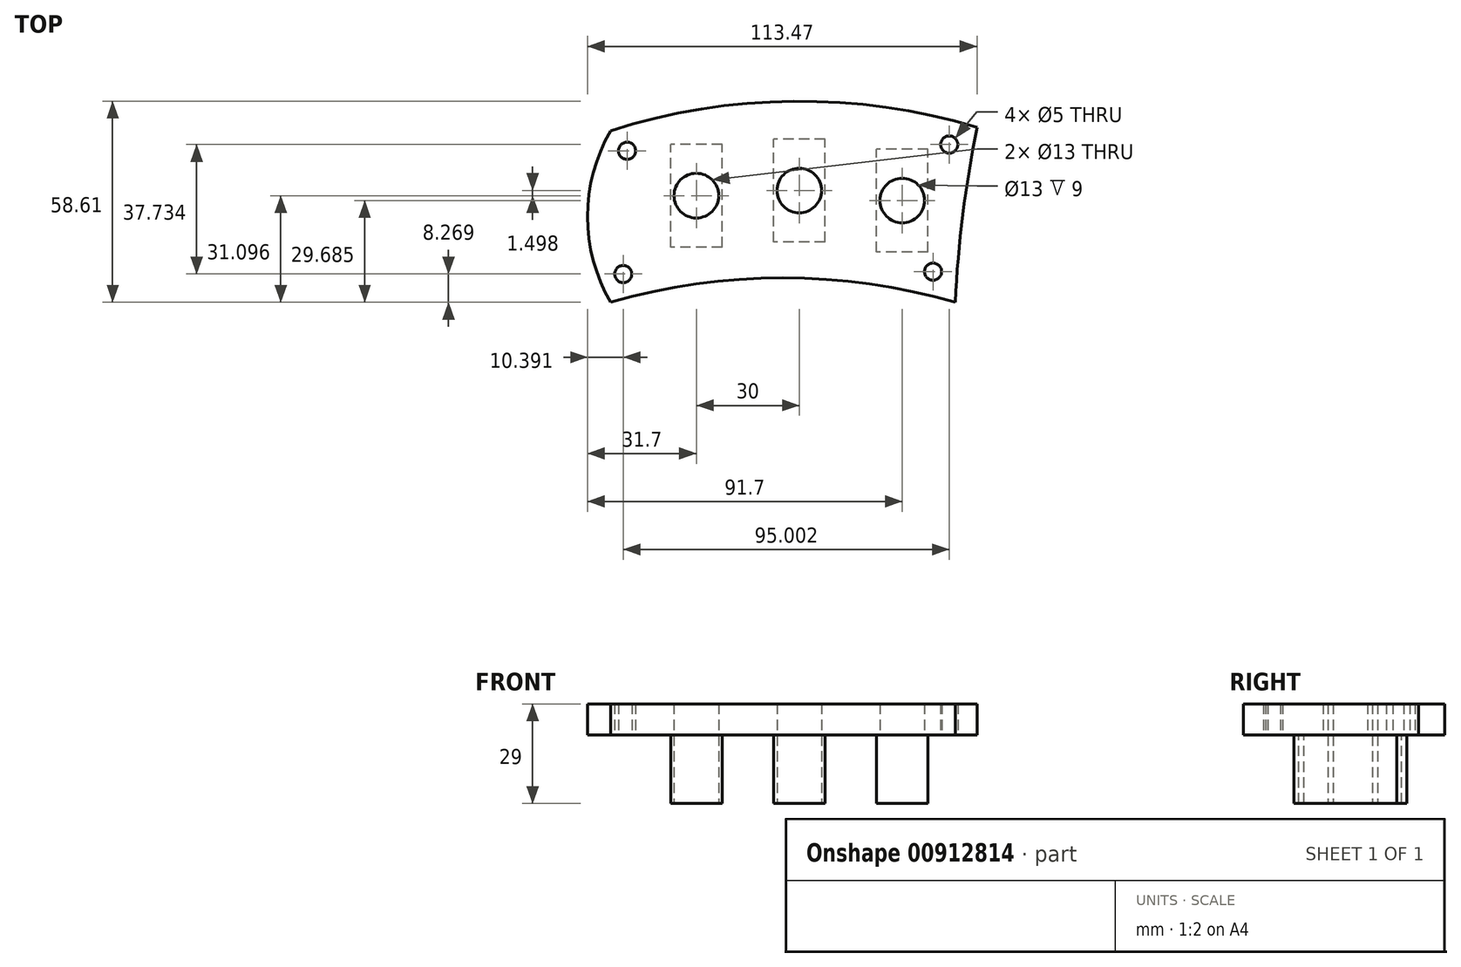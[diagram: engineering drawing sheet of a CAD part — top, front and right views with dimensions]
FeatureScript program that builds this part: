
annotation { "Feature Type Name" : "Feature", "Feature Type Description" : "" }
export const myFeature = defineFeature(function(context is Context, id is Id, definition is map)
    precondition{}
    {
        {
            var Q0;
            Q0=qCreatedBy(makeId("Top.planeOp"),FACE);
            var sketch = newSketch(context, id + "F0", { "sketchPlane" : qUnion([Q0])});
            skCircle(sketch, "E0", {"center": v(0, 0) * mm, "radius": 42.86 * mm, "construction": true});
            skLineSegment(sketch, "E1.bottom", {"start": v(70, 70) * mm, "end": v(-70, 70) * mm, "construction": true});
            skLineSegment(sketch, "E1.top", {"start": v(70, -70) * mm, "end": v(-70, -70) * mm, "construction": true});
            skLineSegment(sketch, "E1.left", {"start": v(70, 70) * mm, "end": v(70, -70) * mm, "construction": true});
            skLineSegment(sketch, "E1.right", {"start": v(-70, 70) * mm, "end": v(-70, -70) * mm, "construction": true});
            skArc(sketch, "E2", {"start": v(70, 70) * mm, "mid": v(0, 88.76) * mm, "end": v(-70, 70) * mm});
            skArc(sketch, "E3", {"start": v(-88.29, 11.48) * mm, "mid": v(-85.36, -30.66) * mm, "end": v(-70, -70) * mm});
            skArc(sketch, "E4", {"start": v(-70, -70) * mm, "mid": v(0, -88.76) * mm, "end": v(70, -70) * mm});
            skArc(sketch, "E5", {"start": v(70, -70) * mm, "mid": v(85.36, -30.66) * mm, "end": v(88.29, 11.48) * mm});
            skLineSegment(sketch, "E6.bottom", {"start": v(55, 55) * mm, "end": v(-55, 55) * mm, "construction": true});
            skLineSegment(sketch, "E6.top", {"start": v(55, -55) * mm, "end": v(-55, -55) * mm, "construction": true});
            skLineSegment(sketch, "E6.left", {"start": v(55, 55) * mm, "end": v(55, -55) * mm, "construction": true});
            skLineSegment(sketch, "E6.right", {"start": v(-55, 55) * mm, "end": v(-55, -55) * mm, "construction": true});
            skCircle(sketch, "E7", {"center": v(-55, 55) * mm, "radius": 2.5 * mm});
            skArc(sketch, "E8", {"start": v(-59.61, 49.09) * mm, "mid": v(-49.7, 49.7) * mm, "end": v(-49.09, 59.61) * mm});
            skCircle(sketch, "E9", {"center": v(55, 55) * mm, "radius": 2.5 * mm});
            skArc(sketch, "E10", {"start": v(49.09, 59.61) * mm, "mid": v(49.7, 49.7) * mm, "end": v(59.61, 49.09) * mm});
            skArc(sketch, "E11", {"start": v(-49.09, -59.61) * mm, "mid": v(-49.7, -49.7) * mm, "end": v(-59.61, -49.09) * mm});
            skCircle(sketch, "E12", {"center": v(-55, -55) * mm, "radius": 2.5 * mm});
            skArc(sketch, "E13", {"start": v(59.61, -49.09) * mm, "mid": v(49.7, -49.7) * mm, "end": v(49.09, -59.61) * mm});
            skCircle(sketch, "E14", {"center": v(55, -55) * mm, "radius": 2.5 * mm});
            skArc(sketch, "E15.0", {"start": v(47.87, 64.23) * mm, "mid": v(0, 73.76) * mm, "end": v(-47.87, 64.23) * mm});
            skArc(sketch, "E15.1", {"start": v(64.23, -47.87) * mm, "mid": v(73.76, 0) * mm, "end": v(64.23, 47.87) * mm});
            skArc(sketch, "E15.2", {"start": v(-47.87, -64.23) * mm, "mid": v(0, -73.76) * mm, "end": v(47.87, -64.23) * mm});
            skArc(sketch, "E15.3", {"start": v(-64.23, 47.87) * mm, "mid": v(-73.76, 0) * mm, "end": v(-64.23, -47.87) * mm});
            skArc(sketch, "E16", {"start": v(109.94, -69.44) * mm, "mid": v(105.48, -27.66) * mm, "end": v(94.08, 12.78) * mm});
            skArc(sketch, "E17.0", {"start": v(209.56, -57.5) * mm, "mid": v(193.7, 30.58) * mm, "end": v(156, 111.76) * mm});
            skCircle(sketch, "E18.0", {"center": v(-140, -75) * mm, "radius": 300 * mm, "construction": true});
            skCircle(sketch, "E19", {"center": v(132.72, 50) * mm, "radius": 26.2 * mm, "construction": true});
            skCircle(sketch, "E20", {"center": v(155.8, -25) * mm, "radius": 26.2 * mm, "construction": true});
            skArc(sketch, "E21", {"start": v(156, 111.76) * mm, "mid": v(104.5, 108.03) * mm, "end": v(69.57, 70) * mm});
            skArc(sketch, "E22", {"start": v(109.94, -69.44) * mm, "mid": v(162.27, -84.5) * mm, "end": v(209.56, -57.5) * mm});
            skLineSegment(sketch, "E23", {"start": v(0, 0) * mm, "end": v(0, 164.88) * mm, "construction": true});
            skPoint(sketch, "E23.endSnap0", {"position": v(0, 55) * mm});
            skLineSegment(sketch, "E24", {"start": v(-22.48, 0) * mm, "end": v(0, 0) * mm, "construction": true});
            skArc(sketch, "E25.MirrorC", {"start": v(-109.94, -69.44) * mm, "mid": v(-105.48, -27.66) * mm, "end": v(-94.08, 12.78) * mm});
            skCircle(sketch, "E26.MirrorC", {"center": v(140, -75) * mm, "radius": 300 * mm, "construction": true});
            skArc(sketch, "E27.MirrorC", {"start": v(-209.56, -57.5) * mm, "mid": v(-193.7, 30.58) * mm, "end": v(-156, 111.76) * mm});
            skArc(sketch, "E28.MirrorC", {"start": v(-156, 111.76) * mm, "mid": v(-104.5, 108.03) * mm, "end": v(-69.57, 70) * mm});
            skCircle(sketch, "E29.MirrorC", {"center": v(-132.72, 50) * mm, "radius": 26.2 * mm, "construction": true});
            skArc(sketch, "E30.MirrorC", {"start": v(-109.94, -69.44) * mm, "mid": v(-162.27, -84.5) * mm, "end": v(-209.56, -57.5) * mm});
            skCircle(sketch, "E31.MirrorC", {"center": v(-155.8, -25) * mm, "radius": 26.2 * mm, "construction": true});
            skArc(sketch, "E32.0", {"start": v(-136.64, 99.97) * mm, "mid": v(-109.56, 93.79) * mm, "end": v(-88.95, 75.15) * mm});
            skArc(sketch, "E32.1", {"start": v(-193.47, -43.06) * mm, "mid": v(-179.4, 26.06) * mm, "end": v(-151.15, 90.7) * mm});
            skArc(sketch, "E32.2", {"start": v(-133.65, -66.12) * mm, "mid": v(-161.23, -69.52) * mm, "end": v(-186.94, -59) * mm});
            skArc(sketch, "E32.3", {"start": v(-124, -52.1) * mm, "mid": v(-112.65, 4.94) * mm, "end": v(-89.13, 58.13) * mm});
            skArc(sketch, "E33.0", {"start": v(136.64, 99.97) * mm, "mid": v(109.56, 93.79) * mm, "end": v(88.95, 75.15) * mm});
            skArc(sketch, "E33.1", {"start": v(193.47, -43.06) * mm, "mid": v(179.4, 26.06) * mm, "end": v(151.15, 90.7) * mm});
            skArc(sketch, "E33.2", {"start": v(133.65, -66.12) * mm, "mid": v(161.23, -69.52) * mm, "end": v(186.94, -59) * mm});
            skArc(sketch, "E33.3", {"start": v(124, -52.1) * mm, "mid": v(112.65, 4.94) * mm, "end": v(89.13, 58.13) * mm});
            skArc(sketch, "E34.0", {"start": v(-144.5, 96.12) * mm, "mid": v(-110.94, 91.12) * mm, "end": v(-87.6, 66.5) * mm, "construction": true});
            skArc(sketch, "E34.1", {"start": v(-191.15, -51.32) * mm, "mid": v(-176.53, 25.15) * mm, "end": v(-144.5, 96.12) * mm, "construction": true});
            skArc(sketch, "E34.2", {"start": v(-127.57, -59.82) * mm, "mid": v(-160.83, -66.54) * mm, "end": v(-191.15, -51.32) * mm, "construction": true});
            skArc(sketch, "E34.3", {"start": v(-127.57, -59.82) * mm, "mid": v(-115.52, 5.85) * mm, "end": v(-87.6, 66.5) * mm, "construction": true});
            skArc(sketch, "E35.0", {"start": v(144.5, 96.12) * mm, "mid": v(110.94, 91.12) * mm, "end": v(87.6, 66.5) * mm, "construction": true});
            skArc(sketch, "E35.1", {"start": v(191.15, -51.32) * mm, "mid": v(176.53, 25.15) * mm, "end": v(144.5, 96.12) * mm, "construction": true});
            skArc(sketch, "E35.2", {"start": v(127.57, -59.82) * mm, "mid": v(160.83, -66.54) * mm, "end": v(191.15, -51.32) * mm, "construction": true});
            skArc(sketch, "E35.3", {"start": v(127.57, -59.82) * mm, "mid": v(115.52, 5.85) * mm, "end": v(87.6, 66.5) * mm, "construction": true});
            skCircle(sketch, "E36", {"center": v(-144.5, 96.12) * mm, "radius": 2.5 * mm});
            skArc(sketch, "E37", {"start": v(-147.03, 91.8) * mm, "mid": v(-141.79, 91.92) * mm, "end": v(-139.53, 96.65) * mm});
            skCircle(sketch, "E38", {"center": v(-87.6, 66.5) * mm, "radius": 2.5 * mm});
            skArc(sketch, "E39", {"start": v(-90.02, 70.87) * mm, "mid": v(-92.6, 66.59) * mm, "end": v(-90.18, 62.2) * mm});
            skCircle(sketch, "E40", {"center": v(-191.15, -51.32) * mm, "radius": 2.5 * mm});
            skArc(sketch, "E41", {"start": v(-187.4, -54.62) * mm, "mid": v(-186.52, -49.45) * mm, "end": v(-190.74, -46.34) * mm});
            skCircle(sketch, "E42", {"center": v(-127.57, -59.82) * mm, "radius": 2.5 * mm});
            skArc(sketch, "E43", {"start": v(-127.21, -54.83) * mm, "mid": v(-131.71, -57.02) * mm, "end": v(-132.06, -62.01) * mm});
            skCircle(sketch, "E44", {"center": v(87.6, 66.5) * mm, "radius": 2.5 * mm});
            skArc(sketch, "E45", {"start": v(90.18, 62.2) * mm, "mid": v(92.6, 66.59) * mm, "end": v(90.02, 70.87) * mm});
            skCircle(sketch, "E46", {"center": v(144.5, 96.12) * mm, "radius": 2.5 * mm});
            skArc(sketch, "E47", {"start": v(139.53, 96.65) * mm, "mid": v(141.79, 91.92) * mm, "end": v(147.03, 91.8) * mm});
            skCircle(sketch, "E48", {"center": v(127.57, -59.82) * mm, "radius": 2.5 * mm});
            skArc(sketch, "E49", {"start": v(132.06, -62.01) * mm, "mid": v(131.71, -57.02) * mm, "end": v(127.21, -54.83) * mm});
            skCircle(sketch, "E50", {"center": v(191.15, -51.32) * mm, "radius": 2.5 * mm});
            skArc(sketch, "E51", {"start": v(190.74, -46.34) * mm, "mid": v(186.52, -49.45) * mm, "end": v(187.4, -54.62) * mm});
            skPoint(sketch, "E52.visualSharp", {"position": v(-52.66, 62.12) * mm});
            skArc(sketch, "E52.filletArc", {"start": v(-47.87, 64.23) * mm, "mid": v(-49.62, 62.22) * mm, "end": v(-49.09, 59.61) * mm});
            skPoint(sketch, "E53.visualSharp", {"position": v(-62.12, 52.66) * mm});
            skArc(sketch, "E53.filletArc", {"start": v(-59.61, 49.09) * mm, "mid": v(-62.22, 49.62) * mm, "end": v(-64.23, 47.87) * mm});
            skPoint(sketch, "E54.visualSharp", {"position": v(52.66, 62.12) * mm});
            skArc(sketch, "E54.filletArc", {"start": v(49.09, 59.61) * mm, "mid": v(49.62, 62.22) * mm, "end": v(47.87, 64.23) * mm});
            skPoint(sketch, "E55.visualSharp", {"position": v(62.12, 52.66) * mm});
            skArc(sketch, "E55.filletArc", {"start": v(64.23, 47.87) * mm, "mid": v(62.22, 49.62) * mm, "end": v(59.61, 49.09) * mm});
            skPoint(sketch, "E56.visualSharp", {"position": v(-62.12, -52.66) * mm});
            skArc(sketch, "E56.filletArc", {"start": v(-64.23, -47.87) * mm, "mid": v(-62.22, -49.62) * mm, "end": v(-59.61, -49.09) * mm});
            skPoint(sketch, "E57.visualSharp", {"position": v(-52.66, -62.12) * mm});
            skArc(sketch, "E57.filletArc", {"start": v(-49.09, -59.61) * mm, "mid": v(-49.62, -62.22) * mm, "end": v(-47.87, -64.23) * mm});
            skPoint(sketch, "E58.visualSharp", {"position": v(52.66, -62.12) * mm});
            skArc(sketch, "E58.filletArc", {"start": v(47.87, -64.23) * mm, "mid": v(49.62, -62.22) * mm, "end": v(49.09, -59.61) * mm});
            skPoint(sketch, "E59.visualSharp", {"position": v(62.12, -52.66) * mm});
            skArc(sketch, "E59.filletArc", {"start": v(59.61, -49.09) * mm, "mid": v(62.22, -49.62) * mm, "end": v(64.23, -47.87) * mm});
            skPoint(sketch, "E60.visualSharp", {"position": v(-84.1, 35.82) * mm});
            skArc(sketch, "E60.filletArc", {"start": v(-88.29, 11.48) * mm, "mid": v(-90.62, 14.65) * mm, "end": v(-94.08, 12.78) * mm});
            skPoint(sketch, "E61.visualSharp", {"position": v(84.1, 35.82) * mm});
            skArc(sketch, "E61.filletArc", {"start": v(94.08, 12.78) * mm, "mid": v(90.62, 14.65) * mm, "end": v(88.29, 11.48) * mm});
            skPoint(sketch, "E62.visualSharp", {"position": v(86.71, 71.41) * mm});
            skArc(sketch, "E62.filletArc", {"start": v(88.95, 75.15) * mm, "mid": v(88.55, 72.78) * mm, "end": v(90.02, 70.87) * mm});
            skPoint(sketch, "E63.visualSharp", {"position": v(87.13, 61.52) * mm});
            skArc(sketch, "E63.filletArc", {"start": v(90.18, 62.2) * mm, "mid": v(88.82, 60.38) * mm, "end": v(89.13, 58.13) * mm});
            skPoint(sketch, "E64.visualSharp", {"position": v(140.99, 99.67) * mm});
            skArc(sketch, "E64.filletArc", {"start": v(139.53, 96.65) * mm, "mid": v(138.82, 98.94) * mm, "end": v(136.64, 99.97) * mm});
            skPoint(sketch, "E65.visualSharp", {"position": v(149.13, 94.2) * mm});
            skArc(sketch, "E65.filletArc", {"start": v(151.15, 90.7) * mm, "mid": v(149.32, 92.1) * mm, "end": v(147.03, 91.8) * mm});
            skPoint(sketch, "E66.visualSharp", {"position": v(124.32, -56.02) * mm});
            skArc(sketch, "E66.filletArc", {"start": v(124, -52.1) * mm, "mid": v(125.05, -54.12) * mm, "end": v(127.21, -54.83) * mm});
            skPoint(sketch, "E67.visualSharp", {"position": v(129.67, -64.36) * mm});
            skArc(sketch, "E67.filletArc", {"start": v(132.06, -62.01) * mm, "mid": v(131.96, -64.41) * mm, "end": v(133.65, -66.12) * mm});
            skPoint(sketch, "E68.visualSharp", {"position": v(190.32, -56.25) * mm});
            skArc(sketch, "E68.filletArc", {"start": v(186.94, -59) * mm, "mid": v(188.13, -56.9) * mm, "end": v(187.4, -54.62) * mm});
            skPoint(sketch, "E69.visualSharp", {"position": v(193.84, -47.1) * mm});
            skArc(sketch, "E69.filletArc", {"start": v(190.74, -46.34) * mm, "mid": v(192.79, -45.27) * mm, "end": v(193.47, -43.06) * mm});
            skPoint(sketch, "E70.visualSharp", {"position": v(-87.13, 61.52) * mm});
            skArc(sketch, "E70.filletArc", {"start": v(-89.13, 58.13) * mm, "mid": v(-88.82, 60.38) * mm, "end": v(-90.18, 62.2) * mm});
            skPoint(sketch, "E71.visualSharp", {"position": v(-86.71, 71.41) * mm});
            skArc(sketch, "E71.filletArc", {"start": v(-90.02, 70.87) * mm, "mid": v(-88.55, 72.78) * mm, "end": v(-88.95, 75.15) * mm});
            skPoint(sketch, "E72.visualSharp", {"position": v(-140.99, 99.67) * mm});
            skArc(sketch, "E72.filletArc", {"start": v(-136.64, 99.97) * mm, "mid": v(-138.82, 98.94) * mm, "end": v(-139.53, 96.65) * mm});
            skPoint(sketch, "E73.visualSharp", {"position": v(-149.13, 94.2) * mm});
            skArc(sketch, "E73.filletArc", {"start": v(-147.03, 91.8) * mm, "mid": v(-149.32, 92.1) * mm, "end": v(-151.15, 90.7) * mm});
            skPoint(sketch, "E74.visualSharp", {"position": v(-193.84, -47.1) * mm});
            skArc(sketch, "E74.filletArc", {"start": v(-193.47, -43.06) * mm, "mid": v(-192.79, -45.27) * mm, "end": v(-190.74, -46.34) * mm});
            skPoint(sketch, "E75.visualSharp", {"position": v(-190.32, -56.25) * mm});
            skArc(sketch, "E75.filletArc", {"start": v(-187.4, -54.62) * mm, "mid": v(-188.13, -56.9) * mm, "end": v(-186.94, -59) * mm});
            skPoint(sketch, "E76.visualSharp", {"position": v(-129.67, -64.36) * mm});
            skArc(sketch, "E76.filletArc", {"start": v(-133.65, -66.12) * mm, "mid": v(-131.96, -64.41) * mm, "end": v(-132.06, -62.01) * mm});
            skPoint(sketch, "E77.visualSharp", {"position": v(-124.32, -56.02) * mm});
            skArc(sketch, "E77.filletArc", {"start": v(-127.21, -54.83) * mm, "mid": v(-125.05, -54.12) * mm, "end": v(-124, -52.1) * mm});
            skLineSegment(sketch, "E78.bottom", {"start": v(200, -57.5) * mm, "end": v(310, -57.5) * mm, "construction": true});
            skLineSegment(sketch, "E78.top", {"start": v(200, -7.5) * mm, "end": v(310, -7.5) * mm, "construction": true});
            skLineSegment(sketch, "E78.left", {"start": v(200, -57.5) * mm, "end": v(200, -7.5) * mm, "construction": true});
            skLineSegment(sketch, "E78.right", {"start": v(310, -57.5) * mm, "end": v(310, -7.5) * mm, "construction": true});
            skArc(sketch, "E79", {"start": v(310, -7.5) * mm, "mid": v(256.7, 1.1) * mm, "end": v(203.23, -6.5) * mm});
            skArc(sketch, "E80", {"start": v(310, -57.5) * mm, "mid": v(316.7, -32.5) * mm, "end": v(310, -7.5) * mm});
            skPoint(sketch, "E81.centerSnap0", {"position": v(200, -32.5) * mm});
            skPoint(sketch, "E82.centerSnap0", {"position": v(255, -7.5) * mm});
            skArc(sketch, "E83", {"start": v(310, -57.5) * mm, "mid": v(259.78, -50.35) * mm, "end": v(209.56, -57.5) * mm});
            skArc(sketch, "E84.0", {"start": v(317.11, -33.01) * mm, "mid": v(259.78, -24.85) * mm, "end": v(202.45, -33.01) * mm, "construction": true});
            skCircle(sketch, "E85", {"center": v(255, -24.9) * mm, "radius": 6.5 * mm});
            skCircle(sketch, "E86", {"center": v(225, -27.82) * mm, "radius": 6.5 * mm});
            skCircle(sketch, "E87", {"center": v(285, -26.4) * mm, "radius": 6.5 * mm});
            skArc(sketch, "E88.0", {"start": v(216.55, -57.15) * mm, "mid": v(214.25, -30.76) * mm, "end": v(210, -4.6) * mm, "construction": true});
            skArc(sketch, "E89.0", {"start": v(305.2, -13.33) * mm, "mid": v(255.23, -5.89) * mm, "end": v(205.24, -13.2) * mm, "construction": true});
            skArc(sketch, "E89.1", {"start": v(306.3, -49.23) * mm, "mid": v(309.68, -31.16) * mm, "end": v(305.2, -13.33) * mm, "construction": true});
            skArc(sketch, "E89.2", {"start": v(306.3, -49.23) * mm, "mid": v(256.86, -43.37) * mm, "end": v(207.6, -50.78) * mm, "construction": true});
            skCircle(sketch, "E90", {"center": v(211.3, -11.5) * mm, "radius": 2.5 * mm});
            skCircle(sketch, "E91", {"center": v(216.02, -48.54) * mm, "radius": 2.5 * mm});
            skCircle(sketch, "E92", {"center": v(306.3, -49.23) * mm, "radius": 2.5 * mm});
            skCircle(sketch, "E93", {"center": v(305.2, -13.33) * mm, "radius": 2.5 * mm});
            skCircle(sketch, "E94.MirrorC", {"center": v(-225, -27.82) * mm, "radius": 6.5 * mm});
            skCircle(sketch, "E95.MirrorC", {"center": v(-255, -24.9) * mm, "radius": 6.5 * mm});
            skCircle(sketch, "E96.MirrorC", {"center": v(-285, -26.4) * mm, "radius": 6.5 * mm});
            skArc(sketch, "E97.MirrorCS", {"start": v(-306.3, -49.23) * mm, "mid": v(-309.68, -31.16) * mm, "end": v(-305.2, -13.33) * mm, "construction": true});
            skCircle(sketch, "E98.MirrorC", {"center": v(-305.2, -13.33) * mm, "radius": 2.5 * mm});
            skArc(sketch, "E99.MirrorCS", {"start": v(-305.2, -13.33) * mm, "mid": v(-255.23, -5.89) * mm, "end": v(-205.24, -13.2) * mm, "construction": true});
            skArc(sketch, "E100.MirrorCS", {"start": v(-216.55, -57.15) * mm, "mid": v(-214.25, -30.76) * mm, "end": v(-210, -4.6) * mm, "construction": true});
            skArc(sketch, "E101.MirrorCS", {"start": v(-306.3, -49.23) * mm, "mid": v(-256.86, -43.37) * mm, "end": v(-207.6, -50.78) * mm, "construction": true});
            skCircle(sketch, "E102.MirrorC", {"center": v(-216.02, -48.54) * mm, "radius": 2.5 * mm});
            skArc(sketch, "E103.MirrorCS", {"start": v(-310, -57.5) * mm, "mid": v(-259.78, -50.35) * mm, "end": v(-209.56, -57.5) * mm});
            skCircle(sketch, "E104.MirrorC", {"center": v(-306.3, -49.23) * mm, "radius": 2.5 * mm});
            skArc(sketch, "E105.MirrorCS", {"start": v(-310, -57.5) * mm, "mid": v(-316.7, -32.5) * mm, "end": v(-310, -7.5) * mm});
            skArc(sketch, "E106.MirrorCS", {"start": v(-310, -7.5) * mm, "mid": v(-256.7, 1.1) * mm, "end": v(-203.23, -6.5) * mm});
            skCircle(sketch, "E107.MirrorC", {"center": v(-211.3, -11.5) * mm, "radius": 2.5 * mm});
            skArc(sketch, "E108.0", {"start": v(152.13, 106.65) * mm, "mid": v(104.88, 101.5) * mm, "end": v(74.22, 65.17) * mm});
            skArc(sketch, "E109.0", {"start": v(203.45, -55.55) * mm, "mid": v(187.97, 28.77) * mm, "end": v(152.13, 106.65) * mm});
            skArc(sketch, "E110.0", {"start": v(115.86, -66.44) * mm, "mid": v(104.07, 2.23) * mm, "end": v(74.22, 65.17) * mm});
            skArc(sketch, "E111.0", {"start": v(115.86, -66.44) * mm, "mid": v(161.83, -78.51) * mm, "end": v(203.45, -55.55) * mm});
            skArc(sketch, "E112.0", {"start": v(128.24, 68.04) * mm, "mid": v(124.5, 66.6) * mm, "end": v(121.04, 64.55) * mm});
            skArc(sketch, "E112.1", {"start": v(161.7, -37.7) * mm, "mid": v(149.84, 16.7) * mm, "end": v(128.24, 68.04) * mm});
            skArc(sketch, "E112.2", {"start": v(153.8, -39) * mm, "mid": v(157.8, -38.69) * mm, "end": v(161.7, -37.7) * mm});
            skArc(sketch, "E112.3", {"start": v(153.8, -39) * mm, "mid": v(142.21, 14.3) * mm, "end": v(121.04, 64.55) * mm});
            skArc(sketch, "E113.MirrorCS", {"start": v(-152.13, 106.65) * mm, "mid": v(-104.88, 101.5) * mm, "end": v(-74.22, 65.17) * mm});
            skArc(sketch, "E114.MirrorCS", {"start": v(-203.45, -55.55) * mm, "mid": v(-187.97, 28.77) * mm, "end": v(-152.13, 106.65) * mm});
            skArc(sketch, "E115.MirrorCS", {"start": v(-115.86, -66.44) * mm, "mid": v(-104.07, 2.23) * mm, "end": v(-74.22, 65.17) * mm});
            skArc(sketch, "E116.MirrorCS", {"start": v(-115.86, -66.44) * mm, "mid": v(-161.83, -78.51) * mm, "end": v(-203.45, -55.55) * mm});
            skArc(sketch, "E117.MirrorCS", {"start": v(-161.7, -37.7) * mm, "mid": v(-149.84, 16.7) * mm, "end": v(-128.24, 68.04) * mm});
            skArc(sketch, "E118.MirrorCS", {"start": v(-153.8, -39) * mm, "mid": v(-157.8, -38.69) * mm, "end": v(-161.7, -37.7) * mm});
            skArc(sketch, "E119.MirrorCS", {"start": v(-153.8, -39) * mm, "mid": v(-142.21, 14.3) * mm, "end": v(-121.04, 64.55) * mm});
            skArc(sketch, "E120.MirrorCS", {"start": v(-128.24, 68.04) * mm, "mid": v(-124.5, 66.6) * mm, "end": v(-121.04, 64.55) * mm});
            skSolve(sketch);
        }
        {
            var Q0;
            Q0=makeQuery(id+"F0.imprint","IMPRINT",FACE,{"disambiguationData":[TD([[makeQuery(id+"F0.imprint","IMPRINT",EDGE,{"derivedFrom":sQuery(id+"F0.wireOp",EDGE,"E96.MirrorC")}),-1.0]])]});
            var Q1;
            Q1=makeQuery(id+"F0.imprint","IMPRINT",FACE,{"disambiguationData":[TD([[makeQuery(id+"F0.imprint","IMPRINT",EDGE,{"derivedFrom":sQuery(id+"F0.wireOp",EDGE,"E95.MirrorC")}),-1.0]])]});
            var Q2;
            Q2=makeQuery(id+"F0.imprint","IMPRINT",FACE,{"disambiguationData":[TD([[makeQuery(id+"F0.imprint","IMPRINT",EDGE,{"derivedFrom":sQuery(id+"F0.wireOp",EDGE,"E94.MirrorC")}),-1.0]])]});
            extrude(context, id + "F1", {"entities" : qUnion([Q0, Q1, Q2]), "depth" : 4.5 * mm, "offsetDistance" : 25 * mm});
        }
        {
            var Q0;
            Q0=makeQuery(id+"F0.imprint","IMPRINT",FACE,{"disambiguationData":[TD([[makeQuery(id+"F0.imprint","IMPRINT",EDGE,{"derivedFrom":sQuery(id+"F0.wireOp",EDGE,"E94.MirrorC")}),-1.0]])]});
            var Q1;
            Q1=makeQuery(id+"F0.imprint","IMPRINT",FACE,{"disambiguationData":[TD([[makeQuery(id+"F0.imprint","IMPRINT",EDGE,{"derivedFrom":sQuery(id+"F0.wireOp",EDGE,"E95.MirrorC")}),-1.0]])]});
            var Q2;
            Q2=makeQuery(id+"F0.imprint","IMPRINT",FACE,{"disambiguationData":[TD([[makeQuery(id+"F0.imprint","IMPRINT",EDGE,{"derivedFrom":sQuery(id+"F0.wireOp",EDGE,"E96.MirrorC")}),-1.0]])]});
            extrude(context, id + "F2", {"entities" : qUnion([Q0, Q1, Q2]), "operationType" : NewBodyOperationType.ADD, "oppositeDirection" : true, "depth" : 4.5 * mm, "offsetDistance" : 25 * mm});
        }
        {
            var Q0;
            Q0=makeQuery(id+"F2.opExtrude","CAP_FACE",FACE,{"disambiguationData":[OSD([sQuery(id+"F0.wireOp",EDGE,"E96.MirrorC")])],"isStart":false});
            var sketch = newSketch(context, id + "F3", { "sketchPlane" : qUnion([Q0])});
            skLineSegment(sketch, "E121.bottom", {"start": v(-277.5, 41.4) * mm, "end": v(-292.5, 41.4) * mm});
            skLineSegment(sketch, "E121.top", {"start": v(-277.5, 11.4) * mm, "end": v(-292.5, 11.4) * mm});
            skLineSegment(sketch, "E121.left", {"start": v(-277.5, 41.4) * mm, "end": v(-277.5, 11.4) * mm});
            skLineSegment(sketch, "E121.right", {"start": v(-292.5, 41.4) * mm, "end": v(-292.5, 11.4) * mm});
            skPoint(sketch, "E121.middle", {"position": v(-285, 26.4) * mm});
            skSolve(sketch);
        }
        {
            var Q0;
            Q0=makeQuery(id+"F2.opExtrude","CAP_FACE",FACE,{"disambiguationData":[OSD([sQuery(id+"F0.wireOp",EDGE,"E95.MirrorC")])],"isStart":false});
            var sketch = newSketch(context, id + "F4", { "sketchPlane" : qUnion([Q0])});
            skLineSegment(sketch, "E122.bottom", {"start": v(-247.5, 39.9) * mm, "end": v(-262.5, 39.9) * mm});
            skLineSegment(sketch, "E122.top", {"start": v(-247.5, 9.9) * mm, "end": v(-262.5, 9.9) * mm});
            skLineSegment(sketch, "E122.left", {"start": v(-247.5, 39.9) * mm, "end": v(-247.5, 9.9) * mm});
            skLineSegment(sketch, "E122.right", {"start": v(-262.5, 39.9) * mm, "end": v(-262.5, 9.9) * mm});
            skPoint(sketch, "E122.middle", {"position": v(-255, 24.9) * mm});
            skSolve(sketch);
        }
        {
            var Q0;
            Q0=makeQuery(id+"F2.opExtrude","CAP_FACE",FACE,{"disambiguationData":[OSD([sQuery(id+"F0.wireOp",EDGE,"E94.MirrorC")])],"isStart":false});
            var sketch = newSketch(context, id + "F5", { "sketchPlane" : qUnion([Q0])});
            skLineSegment(sketch, "E123.bottom", {"start": v(-217.5, 42.82) * mm, "end": v(-232.5, 42.82) * mm});
            skLineSegment(sketch, "E123.top", {"start": v(-217.5, 12.82) * mm, "end": v(-232.5, 12.82) * mm});
            skLineSegment(sketch, "E123.left", {"start": v(-217.5, 42.82) * mm, "end": v(-217.5, 12.82) * mm});
            skLineSegment(sketch, "E123.right", {"start": v(-232.5, 42.82) * mm, "end": v(-232.5, 12.82) * mm});
            skPoint(sketch, "E123.middle", {"position": v(-225, 27.82) * mm});
            skSolve(sketch);
        }
        {
            var Q0;
            Q0=makeQuery(id+"F3.imprint","IMPRINT",FACE,{"disambiguationData":[TD([[makeQuery(id+"F3.imprint","IMPRINT",EDGE,{"derivedFrom":sQuery(id+"F3.wireOp",EDGE,"E121.bottom")}),1.0]])]});
            var Q1;
            Q1=makeQuery(id+"F3.imprint","IMPRINT",FACE,{"disambiguationData":[TD([[makeQuery(id+"F3.imprint","IMPRINT",EDGE,{"derivedFrom":makeQuery(id+"F2.opExtrude","CAP_EDGE",EDGE,{"disambiguationData":[OSD([sQuery(id+"F0.wireOp",EDGE,"E96.MirrorC")])],"isStart":false})}),1.0]])]});
            var Q2;
            Q2=makeQuery(id+"F4.imprint","IMPRINT",FACE,{"disambiguationData":[TD([[makeQuery(id+"F4.imprint","IMPRINT",EDGE,{"derivedFrom":sQuery(id+"F4.wireOp",EDGE,"E122.bottom")}),1.0]])]});
            var Q3;
            Q3=makeQuery(id+"F4.imprint","IMPRINT",FACE,{"disambiguationData":[TD([[makeQuery(id+"F4.imprint","IMPRINT",EDGE,{"derivedFrom":makeQuery(id+"F2.opExtrude","CAP_EDGE",EDGE,{"disambiguationData":[OSD([sQuery(id+"F0.wireOp",EDGE,"E95.MirrorC")])],"isStart":false})}),1.0]])]});
            var Q4;
            Q4 = qSketchRegion(id + "F5", true);
            extrude(context, id + "F6", {"entities" : qUnion([Q0, Q1, Q2, Q3, Q4]), "operationType" : NewBodyOperationType.ADD, "depth" : 20 * mm, "offsetDistance" : 25 * mm});
        }
    });
